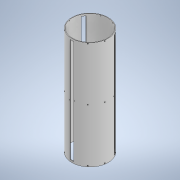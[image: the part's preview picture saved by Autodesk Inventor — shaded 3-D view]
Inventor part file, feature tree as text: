
AUTODESK INVENTOR PART (.ipt)
format: ipt  version: 2021 (Build 250183000, 183)  size: 350,720 bytes
history: native  units: in
note: dims shown in document units (in); Inventor stores cm internally (conversion verified against a paired STEP export)
features: other x34, hole x11, pattern_circular x8, sketch x8, plane x5, extrude x2
ambient origin geometry x8: Origin, YZ Plane, XZ Plane, XY Plane, X Axis, Y Axis, Z Axis, Center Point
bodies: Solid1 (feature_tree)
feature tree (68):
  extrude  "Extrusion1"  Depth=0.3937in
  plane  "Work Plane1"
  extrude  "Extrusion2"  Depth=0.3937in TaperAngle=0.0deg
  pattern_circular  "Circular Pattern1"  Count=3 Angle=360.0deg
  other  "Work Axis1"
  other  "Work Axis2"
  other  "Work Axis3"
  other  "Work Axis4"
  other  "Work Point1"
  other  "Work Point2"
  other  "Work Point3"
  other  "Central Plane"
  other  "Work Point4"
  other  "Work Axis6"
  other  "Work Axis7"
  other  "Offset Plane A"
  other  "Work Point5"
  other  "Work Point6"
  other  "Work Axis8"
  other  "Work Axis9"
  other  "Work Point7"
  other  "Work Point8"
  plane  "Work Plane5"
  plane  "Work Plane6"
  hole  "Hole1"  [1 undecoded]
  hole  "Hole2"  [1 undecoded]
  pattern_circular  "Circular Pattern3"  Count=3 Angle=360.0deg
  sketch  "Sketch5"  dims[d13=0.0484in d14=-11.811in]
  plane  "Work Plane7"
  sketch  "Sketch6"  dims[d15=0.0484in d16=0.1574in]
  hole  "Hole3"  [1 undecoded]
  other  "Work Axis10"
  hole  "Hole4"  [1 undecoded]
  pattern_circular  "Circular Pattern5"  Angle=60.0deg  [1 undecoded]
  plane  "Work Plane12"
  hole  "Hole5"  [1 undecoded]
  pattern_circular  "Circular Pattern6"  [2 undecoded]
  other  "plane for insert hole 1"
  sketch  "Sketch7"  dims[d17=-0.1574in]
  other  "plane for insert hole 2"
  sketch  "Sketch8"  dims[d48=1.0in d49=1.0in d29=0.096in d30=0.75in d31=0.185in d32=0.25in d33=0.5635in d34=1.0in d35=0.0in]
  hole  "insert hole 2"  [1 undecoded]
  hole  "insert hole 1"  [1 undecoded]
  pattern_circular  "Circular Pattern7"  [2 undecoded]
  pattern_circular  "Circular Pattern9"  [2 undecoded]
  other  "Work Axis14"
  other  "Work Axis16"
  other  "Work Point11"
  other  "Work Point12"
  other  "cap hardware plane 1"
  other  "cap hardware plane 2"
  sketch  "Sketch9"  dims[d52=1.0in d53=1.0in d38=0.096in d39=0.75in d40=0.185in d41=0.25in d42=0.5635in d43=1.0in d44=0.8108in d45=1.1811in d46=360.0deg]
  sketch  "Sketch10"  dims[d51=0.38in d54=0.177in d55=0.328in d56=0.332in d57=0.25in d58=0.5635in d59=0.484in d60=0.8108in d64=0.19in d65=0.177in d66=0.3229in d67=0.332in d68=0.25in d69=0.5635in d70=0.484in d71=0.8108in d72=1.5748in d73=360.0deg d75=60.0deg d76=1.0in d77=1.0in d78=0.129in d79=0.3229in d80=0.225in d81=0.25in d82=0.5635in d83=0.484in d84=0.8108in d85=1.1811in d86=360.0deg d88=0.2749in d89=0.2749in d90=0.0in d91=0.0in d92=0.0in d93=11.811in d94=0.0in d95=11.811in d96=0.129in d97=0.224in d98=0.225in d99=0.25in d100=0.5635in d101=0.349in d102=0.8108in d103=0.129in d104=0.224in d105=0.225in d106=0.25in d107=0.5635in d108=0.349in d109=0.8108in d110=1.1811in d111=360.0deg d116=1.1811in d117=360.0deg d119=0.0in d120=30.0deg d121=30.0deg d124=0.1969in d125=23.4252in d126=0.0in d127=0.0in d128=0.1969in d129=23.4252in d147=15.0deg d148=15.0deg d149=0.0in d150=0.0in d151=0.1969in d152=23.4252in d160=0.129in d161=0.75in d162=0.225in d163=0.25in d164=0.5635in d165=0.349in d166=0.8108in d167=0.129in d168=0.75in d169=0.225in d170=0.25in d171=0.5635in d172=0.349in d173=0.8108in d174=1.5748in d175=360.0deg d177=0.0in d178=0.0in d179=11.6142in d180=11.6142in d181=0.0in d182=0.0in d183=11.6142in d184=11.6142in d185=0.129in d186=0.75in d187=0.225in d188=0.25in d189=0.5635in d190=0.349in d191=0.8108in d192=0.129in d193=0.75in d194=0.225in d195=0.25in d196=0.5635in d197=0.349in d198=0.8108in d199=1.1811in d200=360.0deg d61=0.75in d62=0.8108in d63=0.0625in d130=1.0in d131=1.0in d132=1.0in d133=0.15in d134=0.25in d135=0.375in d136=0.5635in d137=0.75in d138=0.8108in d139=0.0625in d140=0.75in d141=0.375in]
  hole  "Quad Symmetry Holes 1"  [1 undecoded]
  hole  "Quad Symmetry Holes 2"  [1 undecoded]
  pattern_circular  "Circular Pattern11"  Count=30  [1 undecoded]
  hole  "Hole13"  [1 undecoded]
  hole  "Hole14"  [1 undecoded]
  pattern_circular  "Circular Pattern12"  [2 undecoded]
  sketch  "Sketch1"  dims[d3=0.0in d5=0.3937in]
  sketch  "Sketch2"  dims[d7=0.3937in d8=0.5in d9=0.0in d10=1.1811in d11=360.0deg]
  other  "Work Axis5"
  other  "Offset Plane B"
  other  "Work Axis11"
  other  "Work Axis12"
  other  "Work Point9"
  other  "Work Axis13"
  other  "Work Point10"
note: 21 required parameter values undecoded (feature->parameter linkage not recoverable at this tier; creation-order binding heuristic only, values carry confidence <= 0.55)
